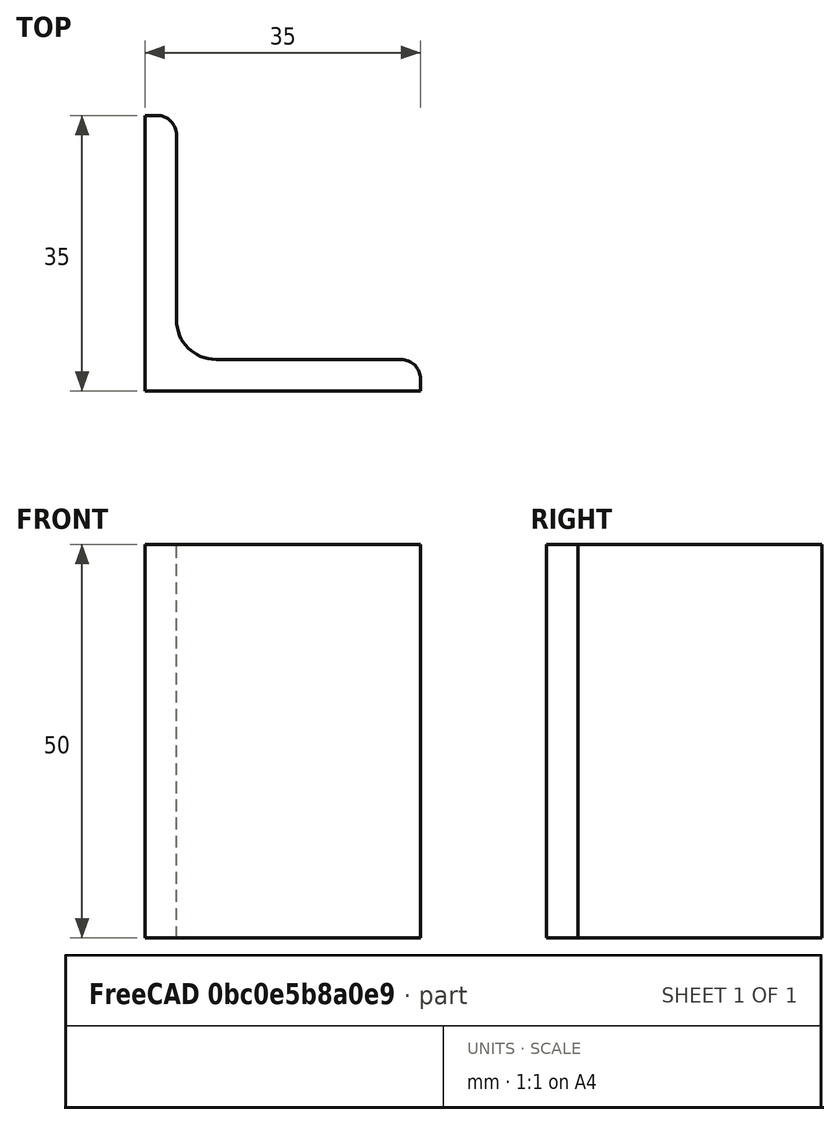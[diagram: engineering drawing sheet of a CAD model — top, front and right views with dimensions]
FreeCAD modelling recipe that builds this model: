
FCSTD DOCUMENT  (FreeCAD 0.15R4671 (Git))
Label: Angle Bar L35x35x4 EN10056 S235JR
License: All rights reserved
LicenseURL: http://en.wikipedia.org/wiki/All_rights_reserved
objects: Sketcher::SketchObject×1, Part::Extrusion×1
note: 2 computed .brp shape members not serialized (recipe doc carries the construction recipe); baked Part::Feature solids carry a one-line shape summary decoded from their .brp

FEATURE [Sketcher::SketchObject] Sketch
  sketch-geometry (9):
    g0: LineSegment StartX=0 StartY=0 StartZ=0 EndX=35 EndY=0 EndZ=0
    g1: LineSegment StartX=35 StartY=0 StartZ=0 EndX=35 EndY=1.5 EndZ=0
    g2: LineSegment StartX=32.5 StartY=4 StartZ=0 EndX=9 EndY=4 EndZ=0
    g3: LineSegment StartX=0 StartY=0 StartZ=0 EndX=0 EndY=35 EndZ=0
    g4: LineSegment StartX=0 StartY=35 StartZ=0 EndX=1.5 EndY=35 EndZ=0
    g5: LineSegment StartX=4 StartY=32.5 StartZ=0 EndX=4 EndY=9 EndZ=0
    g6: ArcOfCircle CenterX=9 CenterY=9 CenterZ=0 NormalX=0 NormalY=0 NormalZ=1 Radius=5 StartAngle=3.14159 EndAngle=4.71239
    g7: ArcOfCircle CenterX=1.5 CenterY=32.5 CenterZ=0 NormalX=0 NormalY=0 NormalZ=1 Radius=2.5 StartAngle=0 EndAngle=1.5708
    g8: ArcOfCircle CenterX=32.5 CenterY=1.5 CenterZ=0 NormalX=0 NormalY=0 NormalZ=1 Radius=2.5 StartAngle=0 EndAngle=1.5708
  constraints (23):
    c: Coincident(g0,g-1)
    c: Horizontal(g0)
    c: Coincident(g1,g0)
    c: Vertical(g1)
    c: Horizontal(g2)
    c: Coincident(g3,g-1)
    c: Vertical(g3)
    c: Coincident(g4,g3)
    c: Horizontal(g4)
    c: Vertical(g5)
    c: Tangent(g5,g6) = -1.5708
    c: Tangent(g2,g6) = 1.5708
    c: Tangent(g4,g7) = 1.5708
    c: Tangent(g5,g7) = 1.5708
    c: Tangent(g2,g8) = -1.5708
    c: Tangent(g1,g8) = -1.5708
    c: DistanceX(g0) = 35
    c: DistanceY(g3) = 35
    c: DistanceY(g0,g2) = 4
    c: DistanceX(g3,g5) = 4
    c: Radius(g6) = 5
    c: Radius(g8) = 2.5
    c: Radius(g7) = 2.5
FEATURE [Part::Extrusion] Extrude  label="Angle Bar L35x35x4 EN10056 S235JR"
  Base = -> Sketch
  Dir = (0,0,50)
  Solid = true
